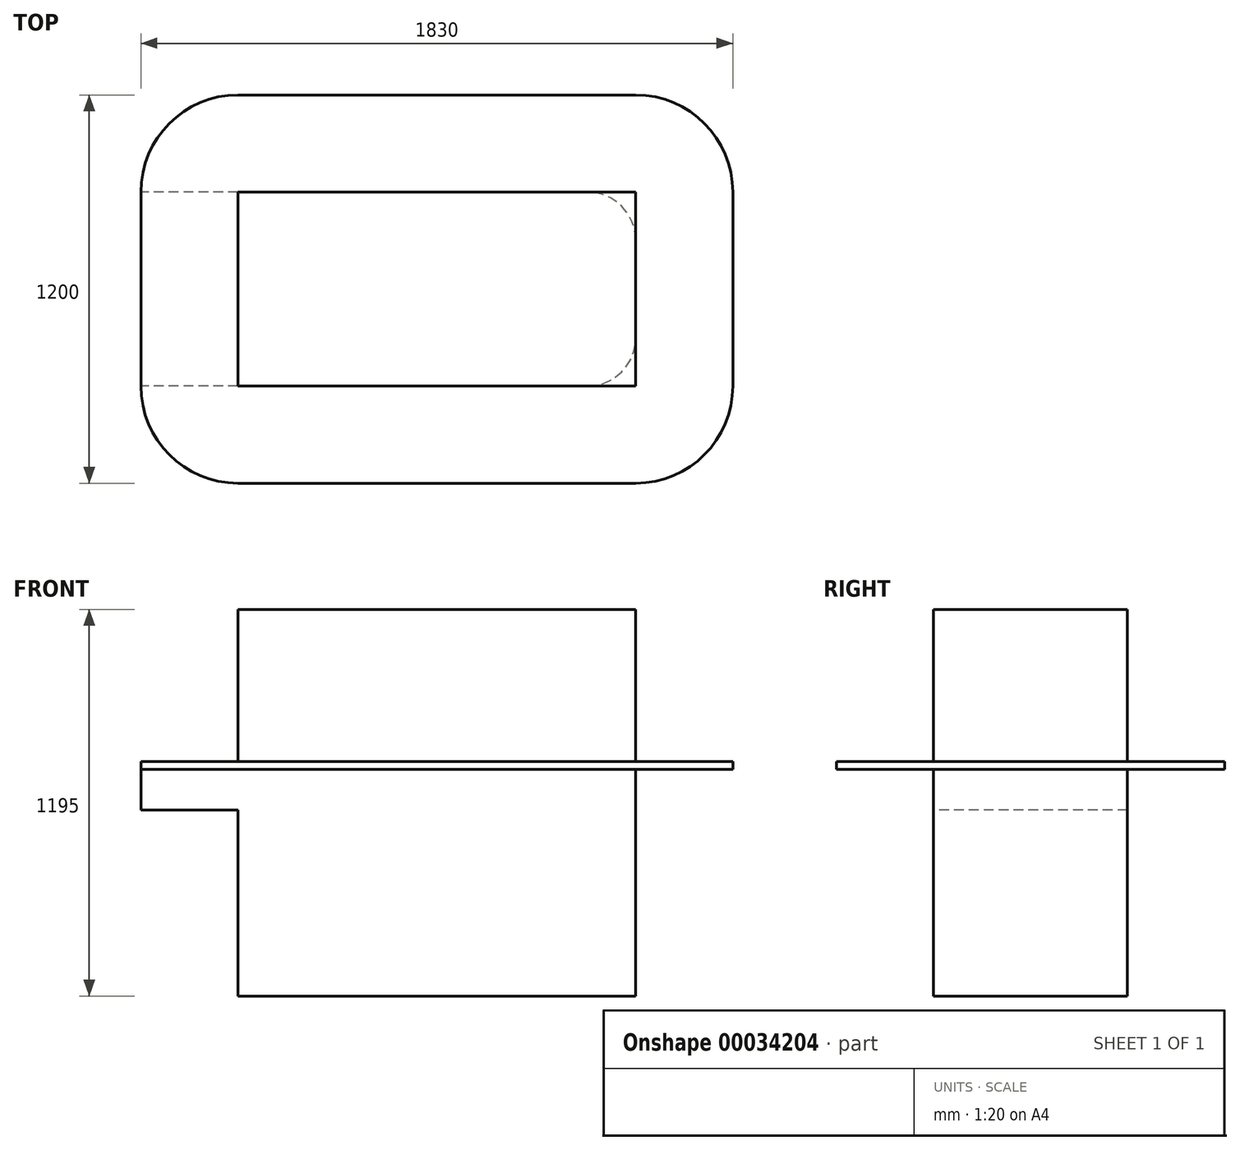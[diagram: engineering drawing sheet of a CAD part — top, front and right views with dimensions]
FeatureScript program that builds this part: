
annotation { "Feature Type Name" : "Feature", "Feature Type Description" : "" }
export const myFeature = defineFeature(function(context is Context, id is Id, definition is map)
    precondition{}
    {
        {
            var Q0;
            Q0=qCreatedBy(makeId("Top.planeOp"),FACE);
            var sketch = newSketch(context, id + "F0", { "sketchPlane" : qUnion([Q0])});
            skLineSegment(sketch, "E0.rect.bottom", {"start": v(615, 300) * mm, "end": v(-615, 300) * mm});
            skLineSegment(sketch, "E0.rect.top", {"start": v(615, -300) * mm, "end": v(-615, -300) * mm});
            skLineSegment(sketch, "E0.rect.left", {"start": v(615, 300) * mm, "end": v(615, -300) * mm});
            skLineSegment(sketch, "E0.rect.right", {"start": v(-615, 300) * mm, "end": v(-615, -300) * mm});
            skPoint(sketch, "E0.rect.middle", {"position": v(0, 0) * mm});
            skSolve(sketch);
        }
        {
            var Q0;
            Q0=makeQuery(id+"F0.imprint","IMPRINT",FACE,{"disambiguationData":[TD([[makeQuery(id+"F0.imprint","IMPRINT",EDGE,{"derivedFrom":sQuery(id+"F0.wireOp",EDGE,"E0.rect.bottom")}),1.0]])]});
            extrude(context, id + "F1", {"entities" : qUnion([Q0]), "depth" : 470 * mm});
        }
        {
            var Q0;
            Q0=makeQuery(id+"F1.opExtrude","CAP_FACE",FACE,{"disambiguationData":[OSD([sQuery(id+"F0.wireOp",EDGE,"E0.rect.bottom"),sQuery(id+"F0.wireOp",EDGE,"E0.rect.top"),sQuery(id+"F0.wireOp",EDGE,"E0.rect.left"),sQuery(id+"F0.wireOp",EDGE,"E0.rect.right")])],"isStart":true});
            var sketch = newSketch(context, id + "F2", { "sketchPlane" : qUnion([Q0])});
            skLineSegment(sketch, "E1.rect.bottom", {"start": v(-615, 600) * mm, "end": v(615, 600) * mm});
            skLineSegment(sketch, "E1.rect.top", {"start": v(-615, -600) * mm, "end": v(615, -600) * mm});
            skLineSegment(sketch, "E1.rect.left", {"start": v(-915, 300) * mm, "end": v(-915, -300) * mm});
            skLineSegment(sketch, "E1.rect.right", {"start": v(915, 300) * mm, "end": v(915, -300) * mm});
            skPoint(sketch, "E1.rect.middle", {"position": v(0, 0) * mm});
            skPoint(sketch, "E2.visualSharp", {"position": v(-915, 600) * mm});
            skArc(sketch, "E2.filletArc", {"start": v(-615, 600) * mm, "mid": v(-827.13, 512.13) * mm, "end": v(-915, 300) * mm});
            skPoint(sketch, "E3.visualSharp", {"position": v(915, 600) * mm});
            skArc(sketch, "E3.filletArc", {"start": v(915, 300) * mm, "mid": v(827.13, 512.13) * mm, "end": v(615, 600) * mm});
            skPoint(sketch, "E4.visualSharp", {"position": v(915, -600) * mm});
            skArc(sketch, "E4.filletArc", {"start": v(615, -600) * mm, "mid": v(827.13, -512.13) * mm, "end": v(915, -300) * mm});
            skPoint(sketch, "E5.visualSharp", {"position": v(-915, -600) * mm});
            skArc(sketch, "E5.filletArc", {"start": v(-915, -300) * mm, "mid": v(-827.13, -512.13) * mm, "end": v(-615, -600) * mm});
            skLineSegment(sketch, "E6", {"start": v(-615, -300) * mm, "end": v(-915, -300) * mm});
            skLineSegment(sketch, "E7", {"start": v(-615, 300) * mm, "end": v(-915, 300) * mm});
            skSolve(sketch);
        }
        {
            var Q0;
            Q0=makeQuery(id+"F2.imprint","IMPRINT",FACE,{"disambiguationData":[TD([[makeQuery(id+"F2.imprint","IMPRINT",EDGE,{"derivedFrom":sQuery(id+"F2.wireOp",EDGE,"E1.rect.bottom")}),-1.0]])]});
            var Q1;
            Q1=makeQuery(id+"F2.imprint","IMPRINT",FACE,{"disambiguationData":[TD([[makeQuery(id+"F2.imprint","IMPRINT",EDGE,{"derivedFrom":makeQuery(id+"F1.opExtrude","CAP_EDGE",EDGE,{"disambiguationData":[OSD([sQuery(id+"F0.wireOp",EDGE,"E0.rect.bottom")])],"isStart":true})}),-1.0]])]});
            extrude(context, id + "F3", {"entities" : qUnion([Q0, Q1]), "depth" : 25 * mm});
        }
        {
            var Q0;
            Q0=makeQuery(id+"F3.opExtrude","CAP_FACE",FACE,{"disambiguationData":[OSD([sQuery(id+"F2.wireOp",EDGE,"E1.rect.bottom"),sQuery(id+"F2.wireOp",EDGE,"E1.rect.top"),sQuery(id+"F2.wireOp",EDGE,"E1.rect.left"),sQuery(id+"F2.wireOp",EDGE,"E1.rect.right"),sQuery(id+"F2.wireOp",EDGE,"E2.filletArc"),sQuery(id+"F2.wireOp",EDGE,"E3.filletArc"),sQuery(id+"F2.wireOp",EDGE,"E4.filletArc"),sQuery(id+"F2.wireOp",EDGE,"E5.filletArc")])],"isStart":false});
            var sketch = newSketch(context, id + "F4", { "sketchPlane" : qUnion([Q0])});
            skLineSegment(sketch, "E8.rect.bottom", {"start": v(-465, -300) * mm, "end": v(465, -300) * mm});
            skLineSegment(sketch, "E8.rect.top", {"start": v(-465, 300) * mm, "end": v(465, 300) * mm});
            skLineSegment(sketch, "E8.rect.left", {"start": v(-615, -150) * mm, "end": v(-615, 150) * mm});
            skLineSegment(sketch, "E8.rect.right", {"start": v(615, -150) * mm, "end": v(615, 150) * mm});
            skPoint(sketch, "E8.rect.middle", {"position": v(0, 0) * mm});
            skPoint(sketch, "E9.visualSharp", {"position": v(-615, -300) * mm});
            skPoint(sketch, "E10.visualSharp", {"position": v(-615, 300) * mm});
            skPoint(sketch, "E11.visualSharp", {"position": v(615, -300) * mm});
            skArc(sketch, "E11.filletArc", {"start": v(465, -300) * mm, "mid": v(571.07, -256.07) * mm, "end": v(615, -150) * mm});
            skPoint(sketch, "E12.visualSharp", {"position": v(615, 300) * mm});
            skArc(sketch, "E12.filletArc", {"start": v(615, 150) * mm, "mid": v(571.07, 256.07) * mm, "end": v(465, 300) * mm});
            skLineSegment(sketch, "E13", {"start": v(-465, -300) * mm, "end": v(-615, -300) * mm});
            skLineSegment(sketch, "E14", {"start": v(-615, 300) * mm, "end": v(-465, 300) * mm});
            skSolve(sketch);
        }
        {
            var Q0;
            Q0=makeQuery(id+"F4.imprint","IMPRINT",FACE,{"disambiguationData":[TD([[makeQuery(id+"F4.imprint","IMPRINT",EDGE,{"derivedFrom":sQuery(id+"F4.wireOp",EDGE,"E8.rect.bottom")}),1.0]])]});
            extrude(context, id + "F5", {"entities" : qUnion([Q0]), "operationType" : NewBodyOperationType.ADD, "depth" : 700 * mm});
        }
        {
            var Q0;
            Q0=makeQuery(id+"F2.imprint","IMPRINT",FACE,{"disambiguationData":[TD([[makeQuery(id+"F2.imprint","IMPRINT",EDGE,{"derivedFrom":sQuery(id+"F2.wireOp",EDGE,"E1.rect.left")}),1.0]])]});
            extrude(context, id + "F6", {"entities" : qUnion([Q0]), "operationType" : NewBodyOperationType.ADD, "depth" : 150 * mm});
        }
    });
